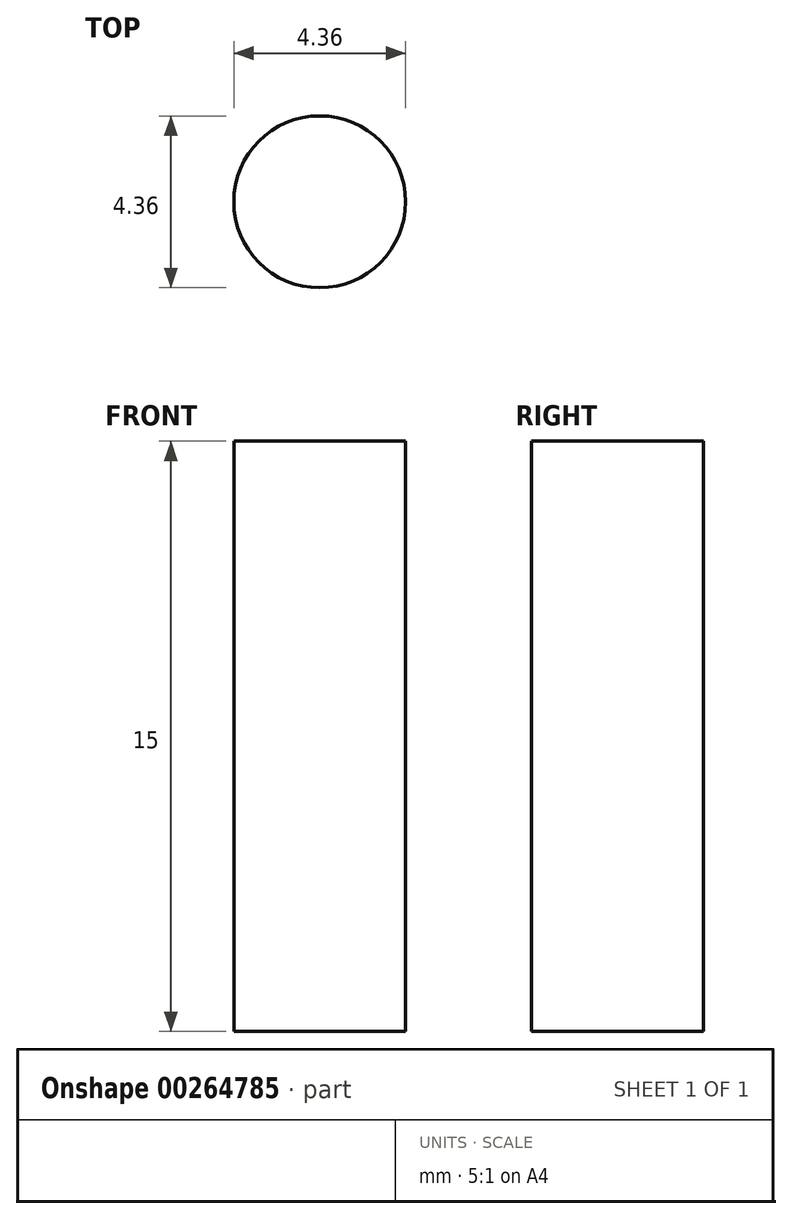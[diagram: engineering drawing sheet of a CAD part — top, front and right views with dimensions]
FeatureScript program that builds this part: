
annotation { "Feature Type Name" : "Feature", "Feature Type Description" : "" }
export const myFeature = defineFeature(function(context is Context, id is Id, definition is map)
    precondition{}
    {
        {
            var Q0;
            Q0=qCreatedBy(makeId("Top.planeOp"),FACE);
            var sketch = newSketch(context, id + "F0", { "sketchPlane" : qUnion([Q0])});
            skCircle(sketch, "E0", {"center": v(0, 0) * mm, "radius": 2.18 * mm});
            skLineSegment(sketch, "E1", {"start": v(-2.18, 0) * mm, "end": v(2.18, 0) * mm, "construction": true});
            skSolve(sketch);
        }
        {
            var Q0;
            Q0=makeQuery(id+"F0.imprint","IMPRINT",FACE,{"disambiguationData":[TD([[makeQuery(id+"F0.imprint","IMPRINT",EDGE,{"derivedFrom":sQuery(id+"F0.wireOp",EDGE,"E0")}),1.0]])]});
            extrude(context, id + "F1", {"entities" : qUnion([Q0]), "depth" : 15 * mm, "offsetDistance" : 25 * mm});
        }
    });
